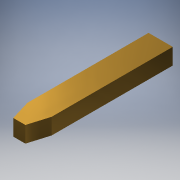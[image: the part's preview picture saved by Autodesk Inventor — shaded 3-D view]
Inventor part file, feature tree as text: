
AUTODESK INVENTOR PART (.ipt)
format: ipt  version: 2018.3 (Build 223284000, 284)  size: 93,696 bytes
history: native  units: mm
features: extrude x1, sketch x1
ambient origin geometry x8: Origin, YZ Plane, XZ Plane, XY Plane, X Axis, Y Axis, Z Axis, Center Point
bodies: Solid1 (feature_tree)
feature tree (2):
  extrude  "Extrusion1"  Depth=0.6mm
  sketch  "Sketch1"  dims[d0=3.0mm d1=0.6mm d2=0.3mm d3=0.5mm d4=0.15mm d5=0.15mm d6=0.4mm d7=0.0mm]
